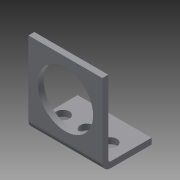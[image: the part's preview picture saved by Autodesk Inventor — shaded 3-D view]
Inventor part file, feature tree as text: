
AUTODESK INVENTOR PART (.ipt)
format: ipt  version: 2013 (Build 170138000, 138)  size: 189,440 bytes
history: native  units: in
note: dims shown in document units (in); Inventor stores cm internally (conversion verified against a paired STEP export)
features: other x5, sheet_metal_op x4, sketch x4, reference x3
ambient origin geometry x8: Origin, YZ Plane, XZ Plane, XY Plane, X Axis, Y Axis, Z Axis, Center Point
bodies: Solid1 (feature_tree)
feature tree (16):
  sheet_metal_op  "Face1"
  sheet_metal_op  "Flange1"
  sketch  "Sketch1"  dims[d0=1.5in]
  other  "Plate1"
  sketch  "Sketch2"  dims[d1=1.5in]
  sketch  "Sketch3"  dims[d2=0.75in]
  other  "Plate2"
  sheet_metal_op  "Bend1"
  sheet_metal_op  "Corner1"
  sketch  "Sketch6"  dims[d3=0.75in d4=0.12in d7=0.75in d8=1.125in d9=0.12in d10=0.0in d11=0.12in d12=0.06in d13=0.24in d14=0.12in d15=1.0in d16=90.0deg d17=0.05in d18=0.48in d19=0.12in d20=0.12in d28=0.12in d29=0.0in d5=0.0in]
  reference  "Reference1"
  reference  "Reference2"
  reference  "Reference3"
  other  "Cut1"
  other  "Cut3"
  other  "Definition1"
